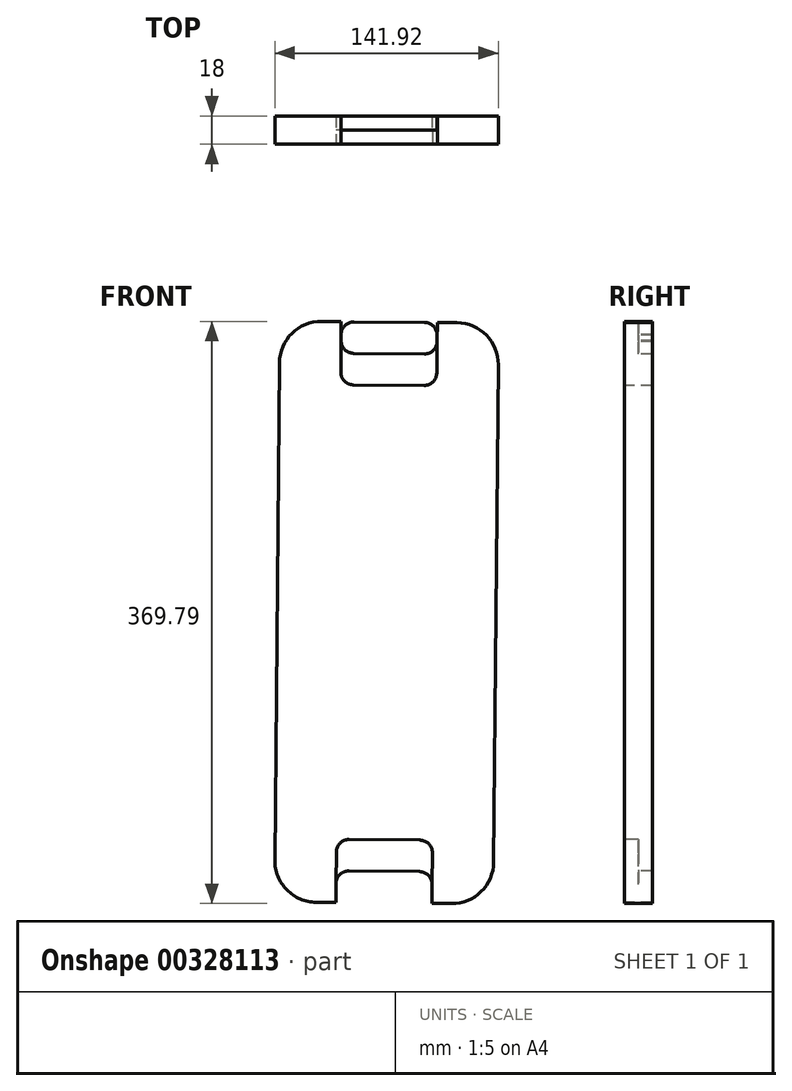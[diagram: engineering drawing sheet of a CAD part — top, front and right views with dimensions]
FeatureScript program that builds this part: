
annotation { "Feature Type Name" : "Feature", "Feature Type Description" : "" }
export const myFeature = defineFeature(function(context is Context, id is Id, definition is map)
    precondition{}
    {
        {
            var Q0;
            Q0=qCreatedBy(makeId("Front.planeOp"),FACE);
            var sketch = newSketch(context, id + "F0", { "sketchPlane" : qUnion([Q0])});
            skLineSegment(sketch, "E0", {"start": v(-90.3, -86.3) * mm, "end": v(-45.3, -86.72) * mm});
            skArc(sketch, "E1", {"start": v(-45.3, -86.72) * mm, "mid": v(-39.66, -89.11) * mm, "end": v(-37.37, -94.8) * mm});
            skLineSegment(sketch, "E2", {"start": v(-37.37, -94.8) * mm, "end": v(-37.49, -106.9) * mm});
            skLineSegment(sketch, "E3", {"start": v(-37.49, -106.9) * mm, "end": v(-24.99, -107.02) * mm});
            skArc(sketch, "E4", {"start": v(-24.99, -107.02) * mm, "mid": v(-6.18, -99.43) * mm, "end": v(1.76, -80.76) * mm});
            skLineSegment(sketch, "E5", {"start": v(1.76, -80.76) * mm, "end": v(4.68, 235.22) * mm});
            skArc(sketch, "E6", {"start": v(4.68, 235.22) * mm, "mid": v(-2.9, 254.03) * mm, "end": v(-21.57, 261.97) * mm});
            skLineSegment(sketch, "E7", {"start": v(-21.57, 261.97) * mm, "end": v(-34.07, 262.08) * mm});
            skLineSegment(sketch, "E8", {"start": v(-34.07, 262.08) * mm, "end": v(-34.18, 249.97) * mm});
            skArc(sketch, "E9", {"start": v(-34.18, 249.97) * mm, "mid": v(-36.58, 244.34) * mm, "end": v(-42.26, 242.05) * mm});
            skLineSegment(sketch, "E10", {"start": v(-42.26, 242.05) * mm, "end": v(-87.25, 242.47) * mm});
            skArc(sketch, "E11", {"start": v(-87.25, 242.47) * mm, "mid": v(-92.89, 244.86) * mm, "end": v(-95.18, 250.54) * mm});
            skLineSegment(sketch, "E12", {"start": v(-95.18, 250.54) * mm, "end": v(-95.07, 262.65) * mm});
            skLineSegment(sketch, "E13", {"start": v(-95.07, 262.65) * mm, "end": v(-107.57, 262.76) * mm});
            skArc(sketch, "E14", {"start": v(-107.57, 262.76) * mm, "mid": v(-126.38, 255.18) * mm, "end": v(-134.31, 236.51) * mm});
            skLineSegment(sketch, "E15", {"start": v(-134.31, 236.51) * mm, "end": v(-137.24, -79.48) * mm});
            skArc(sketch, "E16", {"start": v(-137.24, -79.48) * mm, "mid": v(-129.65, -98.29) * mm, "end": v(-110.98, -106.22) * mm});
            skLineSegment(sketch, "E17", {"start": v(-110.98, -106.22) * mm, "end": v(-98.48, -106.34) * mm});
            skLineSegment(sketch, "E18", {"start": v(-98.48, -106.34) * mm, "end": v(-98.37, -94.23) * mm});
            skArc(sketch, "E19", {"start": v(-98.37, -94.23) * mm, "mid": v(-95.98, -88.6) * mm, "end": v(-90.3, -86.3) * mm});
            skArc(sketch, "E20", {"start": v(-98.4, -98.23) * mm, "mid": v(-96.12, -103.9) * mm, "end": v(-90.48, -106.3) * mm});
            skLineSegment(sketch, "E21", {"start": v(-90.48, -106.3) * mm, "end": v(-45.48, -106.72) * mm});
            skArc(sketch, "E22", {"start": v(-45.48, -106.72) * mm, "mid": v(-39.8, -104.43) * mm, "end": v(-37.41, -98.8) * mm});
            skLineSegment(sketch, "E23", {"start": v(-37.41, -98.8) * mm, "end": v(-37.19, -74.8) * mm});
            skArc(sketch, "E24", {"start": v(-37.19, -74.8) * mm, "mid": v(-39.48, -69.11) * mm, "end": v(-45.11, -66.72) * mm});
            skLineSegment(sketch, "E25", {"start": v(-45.11, -66.72) * mm, "end": v(-90.11, -66.3) * mm});
            skArc(sketch, "E26", {"start": v(-90.11, -66.3) * mm, "mid": v(-95.8, -68.6) * mm, "end": v(-98.19, -74.23) * mm});
            skLineSegment(sketch, "E27", {"start": v(-98.19, -74.23) * mm, "end": v(-98.4, -98.23) * mm});
            skLineSegment(sketch, "E28", {"start": v(-87.07, 262.46) * mm, "end": v(-42.07, 262.05) * mm});
            skArc(sketch, "E29", {"start": v(-42.07, 262.05) * mm, "mid": v(-36.44, 259.65) * mm, "end": v(-34.14, 253.97) * mm});
            skLineSegment(sketch, "E30", {"start": v(-34.14, 253.97) * mm, "end": v(-34.37, 229.98) * mm});
            skArc(sketch, "E31", {"start": v(-34.37, 229.98) * mm, "mid": v(-36.76, 224.34) * mm, "end": v(-42.44, 222.05) * mm});
            skLineSegment(sketch, "E32", {"start": v(-42.44, 222.05) * mm, "end": v(-87.44, 222.47) * mm});
            skArc(sketch, "E33", {"start": v(-87.44, 222.47) * mm, "mid": v(-93.07, 224.86) * mm, "end": v(-95.36, 230.54) * mm});
            skLineSegment(sketch, "E34", {"start": v(-95.36, 230.54) * mm, "end": v(-95.14, 254.54) * mm});
            skArc(sketch, "E35", {"start": v(-95.14, 254.54) * mm, "mid": v(-92.75, 260.17) * mm, "end": v(-87.07, 262.46) * mm});
            skSolve(sketch);
        }
        {
            var Q0;
            {var subQ6=sQuery(id+"F0.wireOp",EDGE,"E2");Q0=makeQuery(id+"F0.imprint","IMPRINT",FACE,{"disambiguationData":[TD([[makeQuery(id+"F0.imprint","IMPRINT",EDGE,{"derivedFrom":subQ6}),1.0]])]});}
            var Q1;
            Q1=makeQuery(id+"F0.imprint","IMPRINT",FACE,{"disambiguationData":[TD([[makeQuery(id+"F0.imprint","IMPRINT",EDGE,{"derivedFrom":sQuery(id+"F0.wireOp",EDGE,"E0")}),1.0]])]});
            var Q2;
            {var subQ1=sQuery(id+"F0.wireOp",EDGE,"E9");Q2=makeQuery(id+"F0.imprint","IMPRINT",FACE,{"disambiguationData":[TD([[makeQuery(id+"F0.imprint","IMPRINT",EDGE,{"derivedFrom":subQ1}),1.0]])]});}
            var Q3;
            Q3 = qConstructionFilter(qBodyType(qCreatedBy(id + "F0" ,EDGE), BodyType.WIRE), ConstructionObject.NO);
            extrude(context, id + "F1", {"entities" : qUnion([Q0, Q1, Q2]), "surfaceEntities" : qUnion([Q3]), "oppositeDirection" : true, "depth" : 18 * mm});
        }
        {
            var Q0;
            Q0=makeQuery(id+"F0.imprint","IMPRINT",FACE,{"disambiguationData":[TD([[makeQuery(id+"F0.imprint","IMPRINT",EDGE,{"derivedFrom":sQuery(id+"F0.wireOp",EDGE,"E0")}),1.0]])]});
            var Q1;
            {var subQ1=sQuery(id+"F0.wireOp",EDGE,"E9");Q1=makeQuery(id+"F0.imprint","IMPRINT",FACE,{"disambiguationData":[TD([[makeQuery(id+"F0.imprint","IMPRINT",EDGE,{"derivedFrom":subQ1}),1.0]])]});}
            extrude(context, id + "F2", {"entities" : qUnion([Q0, Q1]), "operationType" : NewBodyOperationType.REMOVE, "oppositeDirection" : true, "depth" : 9 * mm});
        }
    });
